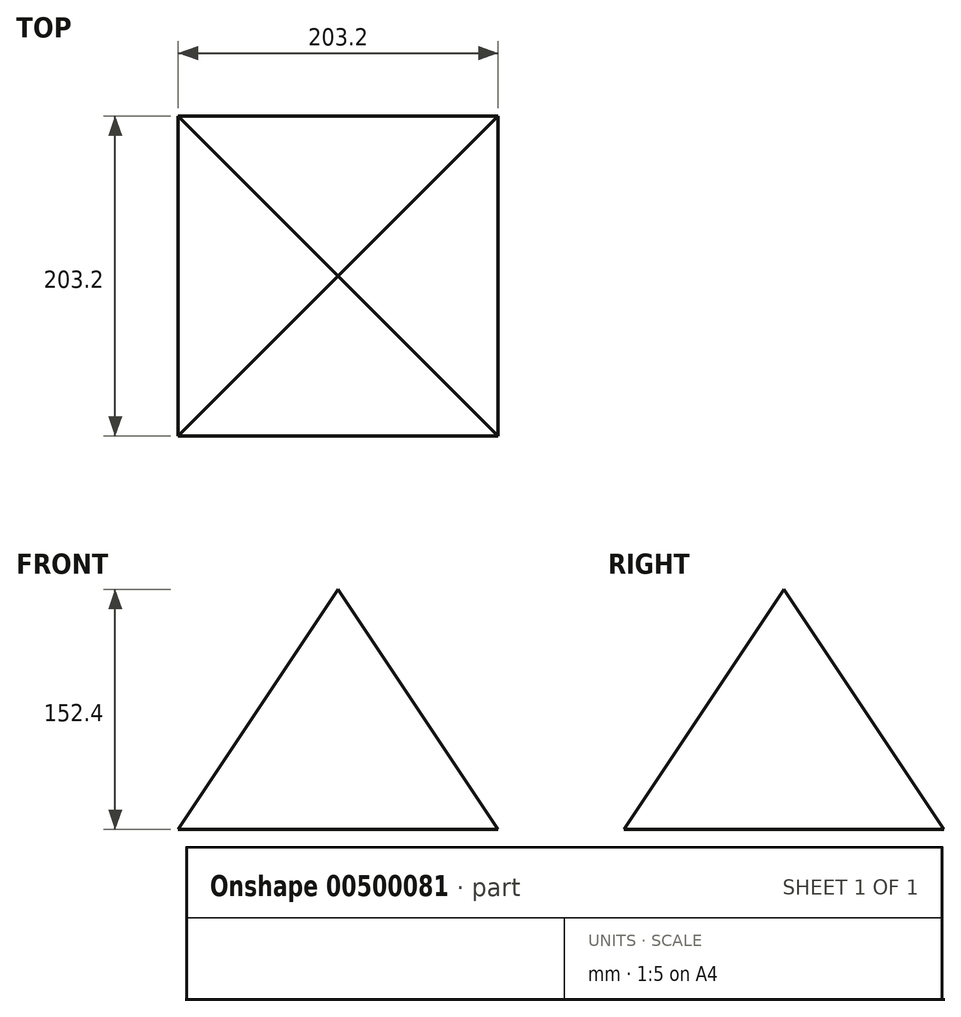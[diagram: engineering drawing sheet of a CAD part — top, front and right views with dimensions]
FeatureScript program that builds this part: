
annotation { "Feature Type Name" : "Feature", "Feature Type Description" : "" }
export const myFeature = defineFeature(function(context is Context, id is Id, definition is map)
    precondition{}
    {
        {
            var Q0;
            Q0=qCreatedBy(makeId("Top.planeOp"),FACE);
            var sketch = newSketch(context, id + "F0", { "sketchPlane" : qUnion([Q0])});
            skLineSegment(sketch, "E0.bottom", {"start": v(-101.6, 101.6) * mm, "end": v(101.6, 101.6) * mm});
            skLineSegment(sketch, "E0.top", {"start": v(-101.6, -101.6) * mm, "end": v(101.6, -101.6) * mm});
            skLineSegment(sketch, "E0.left", {"start": v(-101.6, 101.6) * mm, "end": v(-101.6, -101.6) * mm});
            skLineSegment(sketch, "E0.right", {"start": v(101.6, 101.6) * mm, "end": v(101.6, -101.6) * mm});
            skPoint(sketch, "E0.middle", {"position": v(0, 0) * mm});
            skSolve(sketch);
        }
        {
            var Q0;
            Q0=qCreatedBy(makeId("Top.planeOp"),FACE);
            cPlane(context, id + "F1", {"entities" : qUnion([Q0]), "cplaneType" : CPlaneType.OFFSET, "offset" : 152.4 * mm, "width" : 152.4 * mm, "height" : 152.4 * mm});
        }
        {
            var Q0;
            Q0=qCreatedBy(id+"F1.planeOp",FACE);
            var sketch = newSketch(context, id + "F2", { "sketchPlane" : qUnion([Q0])});
            skPoint(sketch, "E1", {"position": v(0, 0) * mm});
            skSolve(sketch);
        }
        {
            var Q0;
            Q0=makeQuery(id+"F0.imprint","IMPRINT",FACE,{"disambiguationData":[TD([[makeQuery(id+"F0.imprint","IMPRINT",EDGE,{"derivedFrom":sQuery(id+"F0.wireOp",EDGE,"E0.bottom")}),-1.0]])]});
            var Q1;
            Q1=sQuery(id+"F2.wireOp",VERTEX,"E1");
            loft(context, id + "F3", {"sheetProfilesArray" : [{ "sheetProfileEntities" : qUnion([Q0]) }, { "sheetProfileEntities" : qUnion([Q1]) }]});
        }
    });
